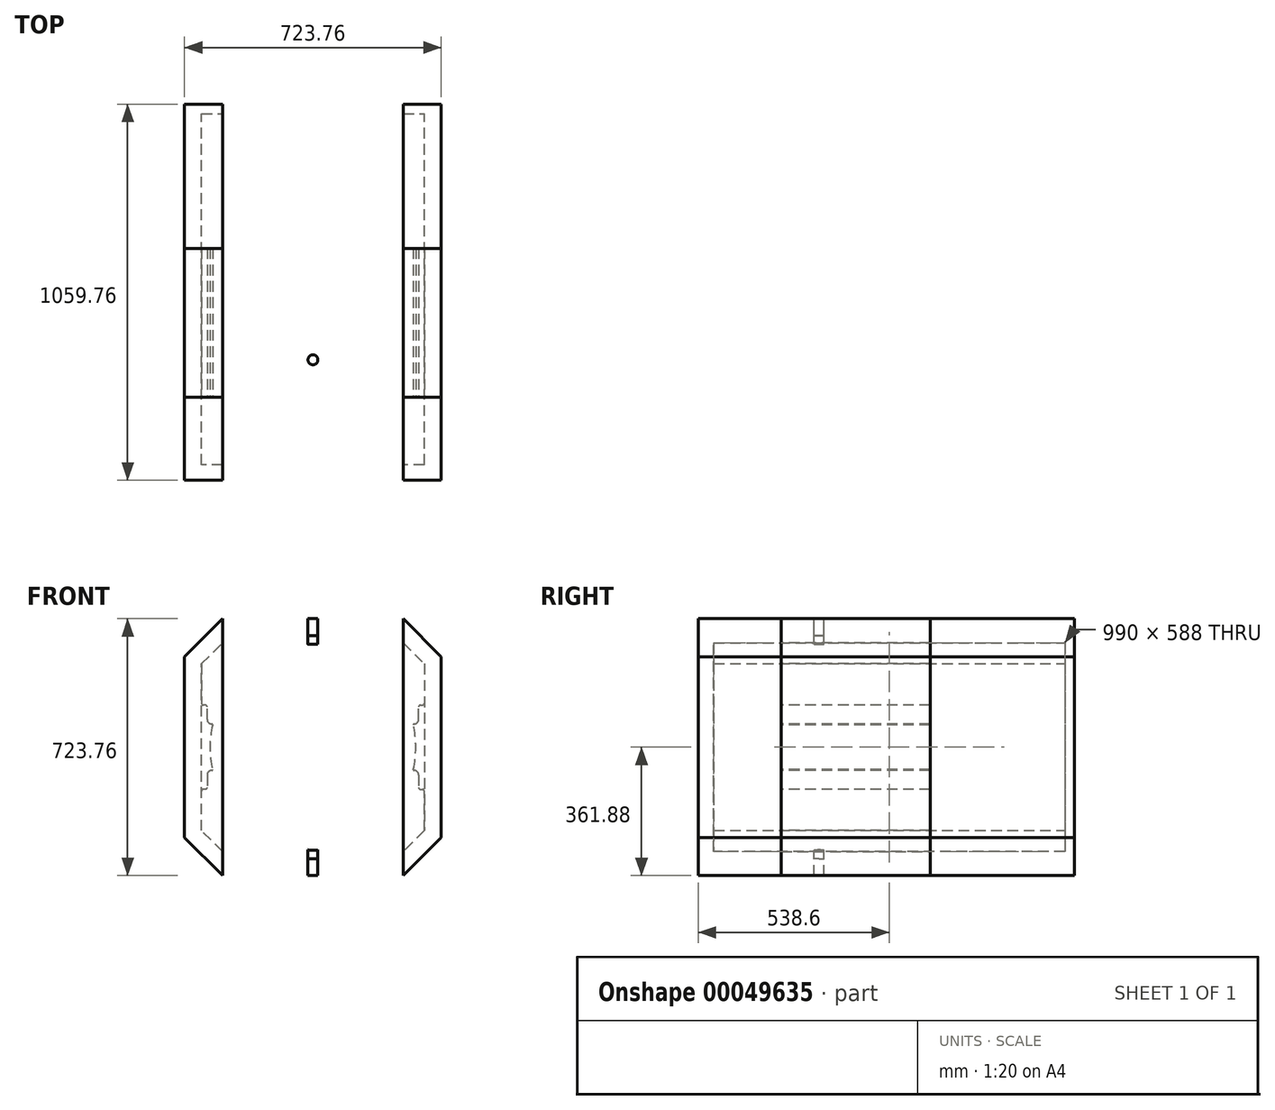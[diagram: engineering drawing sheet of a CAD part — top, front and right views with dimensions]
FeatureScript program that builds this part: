
annotation { "Feature Type Name" : "Feature", "Feature Type Description" : "" }
export const myFeature = defineFeature(function(context is Context, id is Id, definition is map)
    precondition{}
    {
        {
            var Q0;
            Q0=qCreatedBy(makeId("Front.planeOp"),FACE);
            var sketch = newSketch(context, id + "F0", { "sketchPlane" : qUnion([Q0])});
            skLineSegment(sketch, "E0.rect.bottom", {"start": v(-254.77, 361.88) * mm, "end": v(254.77, 361.88) * mm});
            skLineSegment(sketch, "E0.rect.top", {"start": v(-254.77, -361.88) * mm, "end": v(254.77, -361.88) * mm});
            skLineSegment(sketch, "E0.rect.left", {"start": v(-361.88, 254.77) * mm, "end": v(-361.88, -254.77) * mm});
            skLineSegment(sketch, "E0.rect.right", {"start": v(361.88, 254.77) * mm, "end": v(361.88, -254.77) * mm});
            skPoint(sketch, "E0.rect.middle", {"position": v(0, 0) * mm});
            skArc(sketch, "E1", {"start": v(-62.97, -283.02) * mm, "mid": v(-31.67, -288.2) * mm, "end": v(0, -289.94) * mm});
            skLineSegment(sketch, "E2", {"start": v(0, 0) * mm, "end": v(361.88, -361.88) * mm, "construction": true});
            skLineSegment(sketch, "E3", {"start": v(313.88, -234.9) * mm, "end": v(234.9, -313.88) * mm});
            skLineSegment(sketch, "E4", {"start": v(361.88, -254.77) * mm, "end": v(254.77, -361.88) * mm});
            skLineSegment(sketch, "E5.1.0", {"start": v(234.9, 313.88) * mm, "end": v(313.88, 234.9) * mm});
            skLineSegment(sketch, "E5.1.1", {"start": v(254.77, 361.88) * mm, "end": v(361.88, 254.77) * mm});
            skLineSegment(sketch, "E5.2.0", {"start": v(-313.88, 234.9) * mm, "end": v(-234.9, 313.88) * mm});
            skLineSegment(sketch, "E5.2.1", {"start": v(-361.88, 254.77) * mm, "end": v(-254.77, 361.88) * mm});
            skLineSegment(sketch, "E5.3.0", {"start": v(-234.9, -313.88) * mm, "end": v(-313.88, -234.9) * mm});
            skLineSegment(sketch, "E5.3.1", {"start": v(-254.77, -361.88) * mm, "end": v(-361.88, -254.77) * mm});
            skPoint(sketch, "E6.orphan", {"position": v(361.88, 361.88) * mm});
            skPoint(sketch, "E7.orphan", {"position": v(-361.88, 361.88) * mm});
            skPoint(sketch, "E8.orphan", {"position": v(-361.88, -361.88) * mm});
            skLineSegment(sketch, "E9.trimOffspring", {"start": v(-234.9, -313.88) * mm, "end": v(-123.42, -313.88) * mm});
            skCircle(sketch, "E10", {"center": v(0, 0) * mm, "radius": 246.34 * mm, "construction": true});
            skLineSegment(sketch, "E11", {"start": v(0, 0) * mm, "end": v(0, -467.94) * mm, "construction": true});
            skPoint(sketch, "E11.endSnap0", {"position": v(0, -361.88) * mm});
            skLineSegment(sketch, "E12.MirrorCS", {"start": v(-65.4, -284.97) * mm, "end": v(-65.4, -285.17) * mm});
            skLineSegment(sketch, "E13", {"start": v(-78.4, -298.17) * mm, "end": v(-113.42, -298.17) * mm});
            skLineSegment(sketch, "E14", {"start": v(-118.42, -303.17) * mm, "end": v(-118.42, -308.88) * mm});
            skPoint(sketch, "E15.newPointA", {"position": v(-65.4, -313.88) * mm});
            skPoint(sketch, "E15.newPointB", {"position": v(-65.4, -298.17) * mm});
            skArc(sketch, "E15.filletArc", {"start": v(-78.4, -298.17) * mm, "mid": v(-69.2, -294.37) * mm, "end": v(-65.4, -285.17) * mm});
            skPoint(sketch, "E16.visualSharp", {"position": v(-65.4, -282.47) * mm});
            skArc(sketch, "E16.filletArc", {"start": v(-62.97, -283.02) * mm, "mid": v(-64.65, -283.41) * mm, "end": v(-65.4, -284.97) * mm});
            skPoint(sketch, "E17.visualSharp", {"position": v(-118.42, -298.17) * mm});
            skArc(sketch, "E17.filletArc", {"start": v(-113.42, -298.17) * mm, "mid": v(-116.96, -299.64) * mm, "end": v(-118.42, -303.17) * mm});
            skArc(sketch, "E18.filletArc", {"start": v(-123.42, -313.88) * mm, "mid": v(-119.89, -312.42) * mm, "end": v(-118.42, -308.88) * mm});
            skPoint(sketch, "E19.trimOffspring.end.orphan", {"position": v(65.4, -313.88) * mm});
            skPoint(sketch, "E20.orphan", {"position": v(65.4, -282.47) * mm});
            skArc(sketch, "E21.MirrorCS", {"start": v(62.97, -283.02) * mm, "mid": v(31.67, -288.2) * mm, "end": v(0, -289.94) * mm});
            skLineSegment(sketch, "E22.MirrorCS", {"start": v(234.9, -313.88) * mm, "end": v(123.42, -313.88) * mm});
            skArc(sketch, "E23.MirrorCS", {"start": v(123.42, -313.88) * mm, "mid": v(119.89, -312.42) * mm, "end": v(118.42, -308.88) * mm});
            skLineSegment(sketch, "E24.MirrorCS", {"start": v(118.42, -303.17) * mm, "end": v(118.42, -308.88) * mm});
            skArc(sketch, "E25.MirrorCS", {"start": v(113.42, -298.17) * mm, "mid": v(116.96, -299.64) * mm, "end": v(118.42, -303.17) * mm});
            skArc(sketch, "E26.MirrorCS", {"start": v(62.97, -283.02) * mm, "mid": v(64.65, -283.41) * mm, "end": v(65.4, -284.97) * mm});
            skArc(sketch, "E27.MirrorCS", {"start": v(78.4, -298.17) * mm, "mid": v(69.2, -294.37) * mm, "end": v(65.4, -285.17) * mm});
            skLineSegment(sketch, "E28.MirrorCS", {"start": v(78.4, -298.17) * mm, "end": v(113.42, -298.17) * mm});
            skLineSegment(sketch, "E29.1.0", {"start": v(313.88, -234.9) * mm, "end": v(313.88, -123.42) * mm});
            skPoint(sketch, "E29.1.1", {"position": v(313.88, -65.4) * mm});
            skPoint(sketch, "E29.1.2", {"position": v(298.17, -118.42) * mm});
            skPoint(sketch, "E29.1.3", {"position": v(313.88, 65.4) * mm});
            skArc(sketch, "E29.1.4", {"start": v(283.02, -62.97) * mm, "mid": v(288.2, -31.67) * mm, "end": v(289.94, 0) * mm});
            skLineSegment(sketch, "E29.1.5", {"start": v(313.88, 234.9) * mm, "end": v(313.88, 123.42) * mm});
            skPoint(sketch, "E29.1.6", {"position": v(282.47, -65.4) * mm});
            skPoint(sketch, "E29.1.7", {"position": v(282.47, 65.4) * mm});
            skArc(sketch, "E29.1.8", {"start": v(283.02, 62.97) * mm, "mid": v(288.2, 31.67) * mm, "end": v(289.94, 0) * mm});
            skLineSegment(sketch, "E29.1.9", {"start": v(298.17, 78.4) * mm, "end": v(298.17, 113.42) * mm});
            skPoint(sketch, "E29.1.10", {"position": v(298.17, -65.4) * mm});
            skArc(sketch, "E29.1.11", {"start": v(298.17, 113.42) * mm, "mid": v(299.64, 116.96) * mm, "end": v(303.17, 118.42) * mm});
            skLineSegment(sketch, "E29.1.12", {"start": v(303.17, 118.42) * mm, "end": v(308.88, 118.42) * mm});
            skArc(sketch, "E29.1.13", {"start": v(313.88, 123.42) * mm, "mid": v(312.42, 119.89) * mm, "end": v(308.88, 118.42) * mm});
            skLineSegment(sketch, "E29.1.14", {"start": v(298.17, -78.4) * mm, "end": v(298.17, -113.42) * mm});
            skArc(sketch, "E29.1.15", {"start": v(298.17, 78.4) * mm, "mid": v(294.37, 69.2) * mm, "end": v(285.17, 65.4) * mm});
            skArc(sketch, "E29.1.16", {"start": v(283.02, 62.97) * mm, "mid": v(283.41, 64.65) * mm, "end": v(284.97, 65.4) * mm});
            skArc(sketch, "E29.1.17", {"start": v(298.17, -113.42) * mm, "mid": v(299.64, -116.96) * mm, "end": v(303.17, -118.42) * mm});
            skLineSegment(sketch, "E29.1.18", {"start": v(303.17, -118.42) * mm, "end": v(308.88, -118.42) * mm});
            skArc(sketch, "E29.1.19", {"start": v(313.88, -123.42) * mm, "mid": v(312.42, -119.89) * mm, "end": v(308.88, -118.42) * mm});
            skArc(sketch, "E29.1.20", {"start": v(298.17, -78.4) * mm, "mid": v(294.37, -69.2) * mm, "end": v(285.17, -65.4) * mm});
            skLineSegment(sketch, "E29.2.0", {"start": v(234.9, 313.88) * mm, "end": v(123.42, 313.88) * mm});
            skPoint(sketch, "E29.2.1", {"position": v(65.4, 313.88) * mm});
            skPoint(sketch, "E29.2.2", {"position": v(118.42, 298.17) * mm});
            skPoint(sketch, "E29.2.3", {"position": v(-65.4, 313.88) * mm});
            skArc(sketch, "E29.2.4", {"start": v(62.97, 283.02) * mm, "mid": v(31.67, 288.2) * mm, "end": v(0, 289.94) * mm});
            skLineSegment(sketch, "E29.2.5", {"start": v(-234.9, 313.88) * mm, "end": v(-123.42, 313.88) * mm});
            skPoint(sketch, "E29.2.6", {"position": v(65.4, 282.47) * mm});
            skPoint(sketch, "E29.2.7", {"position": v(-65.4, 282.47) * mm});
            skArc(sketch, "E29.2.8", {"start": v(-62.97, 283.02) * mm, "mid": v(-31.67, 288.2) * mm, "end": v(0, 289.94) * mm});
            skLineSegment(sketch, "E29.2.9", {"start": v(-78.4, 298.17) * mm, "end": v(-113.42, 298.17) * mm});
            skPoint(sketch, "E29.2.10", {"position": v(65.4, 298.17) * mm});
            skArc(sketch, "E29.2.11", {"start": v(-113.42, 298.17) * mm, "mid": v(-116.96, 299.64) * mm, "end": v(-118.42, 303.17) * mm});
            skLineSegment(sketch, "E29.2.12", {"start": v(-118.42, 303.17) * mm, "end": v(-118.42, 308.88) * mm});
            skArc(sketch, "E29.2.13", {"start": v(-123.42, 313.88) * mm, "mid": v(-119.89, 312.42) * mm, "end": v(-118.42, 308.88) * mm});
            skLineSegment(sketch, "E29.2.14", {"start": v(78.4, 298.17) * mm, "end": v(113.42, 298.17) * mm});
            skArc(sketch, "E29.2.15", {"start": v(-78.4, 298.17) * mm, "mid": v(-69.2, 294.37) * mm, "end": v(-65.4, 285.17) * mm});
            skArc(sketch, "E29.2.16", {"start": v(-62.97, 283.02) * mm, "mid": v(-64.65, 283.41) * mm, "end": v(-65.4, 284.97) * mm});
            skArc(sketch, "E29.2.17", {"start": v(113.42, 298.17) * mm, "mid": v(116.96, 299.64) * mm, "end": v(118.42, 303.17) * mm});
            skLineSegment(sketch, "E29.2.18", {"start": v(118.42, 303.17) * mm, "end": v(118.42, 308.88) * mm});
            skArc(sketch, "E29.2.19", {"start": v(123.42, 313.88) * mm, "mid": v(119.89, 312.42) * mm, "end": v(118.42, 308.88) * mm});
            skArc(sketch, "E29.2.20", {"start": v(78.4, 298.17) * mm, "mid": v(69.2, 294.37) * mm, "end": v(65.4, 285.17) * mm});
            skLineSegment(sketch, "E29.3.0", {"start": v(-313.88, 234.9) * mm, "end": v(-313.88, 123.42) * mm});
            skPoint(sketch, "E29.3.1", {"position": v(-313.88, 65.4) * mm});
            skPoint(sketch, "E29.3.2", {"position": v(-298.17, 118.42) * mm});
            skPoint(sketch, "E29.3.3", {"position": v(-313.88, -65.4) * mm});
            skArc(sketch, "E29.3.4", {"start": v(-283.02, 62.97) * mm, "mid": v(-288.2, 31.67) * mm, "end": v(-289.94, 0) * mm});
            skLineSegment(sketch, "E29.3.5", {"start": v(-313.88, -234.9) * mm, "end": v(-313.88, -123.42) * mm});
            skPoint(sketch, "E29.3.6", {"position": v(-282.47, 65.4) * mm});
            skPoint(sketch, "E29.3.7", {"position": v(-282.47, -65.4) * mm});
            skArc(sketch, "E29.3.8", {"start": v(-283.02, -62.97) * mm, "mid": v(-288.2, -31.67) * mm, "end": v(-289.94, 0) * mm});
            skLineSegment(sketch, "E29.3.9", {"start": v(-298.17, -78.4) * mm, "end": v(-298.17, -113.42) * mm});
            skPoint(sketch, "E29.3.10", {"position": v(-298.17, 65.4) * mm});
            skArc(sketch, "E29.3.11", {"start": v(-298.17, -113.42) * mm, "mid": v(-299.64, -116.96) * mm, "end": v(-303.17, -118.42) * mm});
            skLineSegment(sketch, "E29.3.12", {"start": v(-303.17, -118.42) * mm, "end": v(-308.88, -118.42) * mm});
            skArc(sketch, "E29.3.13", {"start": v(-313.88, -123.42) * mm, "mid": v(-312.42, -119.89) * mm, "end": v(-308.88, -118.42) * mm});
            skLineSegment(sketch, "E29.3.14", {"start": v(-298.17, 78.4) * mm, "end": v(-298.17, 113.42) * mm});
            skArc(sketch, "E29.3.15", {"start": v(-298.17, -78.4) * mm, "mid": v(-294.37, -69.2) * mm, "end": v(-285.17, -65.4) * mm});
            skArc(sketch, "E29.3.16", {"start": v(-283.02, -62.97) * mm, "mid": v(-283.41, -64.65) * mm, "end": v(-284.97, -65.4) * mm});
            skArc(sketch, "E29.3.17", {"start": v(-298.17, 113.42) * mm, "mid": v(-299.64, 116.96) * mm, "end": v(-303.17, 118.42) * mm});
            skLineSegment(sketch, "E29.3.18", {"start": v(-303.17, 118.42) * mm, "end": v(-308.88, 118.42) * mm});
            skArc(sketch, "E29.3.19", {"start": v(-313.88, 123.42) * mm, "mid": v(-312.42, 119.89) * mm, "end": v(-308.88, 118.42) * mm});
            skArc(sketch, "E29.3.20", {"start": v(-298.17, 78.4) * mm, "mid": v(-294.37, 69.2) * mm, "end": v(-285.17, 65.4) * mm});
            skLineSegment(sketch, "E30", {"start": v(65.4, -284.97) * mm, "end": v(65.4, -285.17) * mm});
            skLineSegment(sketch, "E31", {"start": v(-285.17, -65.4) * mm, "end": v(-284.97, -65.4) * mm});
            skArc(sketch, "E32", {"start": v(-285.17, 65.4) * mm, "mid": v(-283.55, 64.67) * mm, "end": v(-283.02, 62.97) * mm});
            skLineSegment(sketch, "E33", {"start": v(-65.4, 285.17) * mm, "end": v(-65.4, 284.97) * mm});
            skArc(sketch, "E34", {"start": v(62.97, 283.02) * mm, "mid": v(64.73, 283.48) * mm, "end": v(65.4, 285.17) * mm});
            skLineSegment(sketch, "E35", {"start": v(284.97, 65.4) * mm, "end": v(285.17, 65.4) * mm});
            skArc(sketch, "E36", {"start": v(285.17, -65.4) * mm, "mid": v(283.55, -64.67) * mm, "end": v(283.02, -62.97) * mm});
            skSolve(sketch);
        }
        {
            var Q0;
            Q0=makeQuery(id+"F0.imprint","IMPRINT",FACE,{"disambiguationData":[TD([[makeQuery(id+"F0.imprint","IMPRINT",EDGE,{"derivedFrom":sQuery(id+"F0.wireOp",EDGE,"E0.rect.bottom")}),-1.0]])]});
            extrude(context, id + "F1", {"entities" : qUnion([Q0]), "oppositeDirection" : true, "depth" : 420 * mm});
        }
        {
            var Q0;
            Q0=makeQuery(id+"F1.opExtrude","CAP_FACE",FACE,{"disambiguationData":[OSD([sQuery(id+"F0.wireOp",EDGE,"E0.rect.bottom"),sQuery(id+"F0.wireOp",EDGE,"E0.rect.top"),sQuery(id+"F0.wireOp",EDGE,"E0.rect.left"),sQuery(id+"F0.wireOp",EDGE,"E0.rect.right"),sQuery(id+"F0.wireOp",EDGE,"E1"),sQuery(id+"F0.wireOp",EDGE,"E3"),sQuery(id+"F0.wireOp",EDGE,"E4"),sQuery(id+"F0.wireOp",EDGE,"E5.1.0"),sQuery(id+"F0.wireOp",EDGE,"E5.1.1"),sQuery(id+"F0.wireOp",EDGE,"E5.2.0"),sQuery(id+"F0.wireOp",EDGE,"E5.2.1"),sQuery(id+"F0.wireOp",EDGE,"E5.3.0"),sQuery(id+"F0.wireOp",EDGE,"E5.3.1"),sQuery(id+"F0.wireOp",EDGE,"E9.trimOffspring"),sQuery(id+"F0.wireOp",EDGE,"E12.MirrorCS"),sQuery(id+"F0.wireOp",EDGE,"E13"),sQuery(id+"F0.wireOp",EDGE,"E14"),sQuery(id+"F0.wireOp",EDGE,"E15.filletArc"),sQuery(id+"F0.wireOp",EDGE,"E16.filletArc"),sQuery(id+"F0.wireOp",EDGE,"E17.filletArc"),sQuery(id+"F0.wireOp",EDGE,"E18.filletArc"),sQuery(id+"F0.wireOp",EDGE,"E21.MirrorCS"),sQuery(id+"F0.wireOp",EDGE,"E22.MirrorCS"),sQuery(id+"F0.wireOp",EDGE,"E23.MirrorCS"),sQuery(id+"F0.wireOp",EDGE,"E24.MirrorCS"),sQuery(id+"F0.wireOp",EDGE,"E25.MirrorCS"),sQuery(id+"F0.wireOp",EDGE,"E26.MirrorCS"),sQuery(id+"F0.wireOp",EDGE,"E27.MirrorCS"),sQuery(id+"F0.wireOp",EDGE,"E28.MirrorCS"),sQuery(id+"F0.wireOp",EDGE,"E29.1.0"),sQuery(id+"F0.wireOp",EDGE,"E29.1.4"),sQuery(id+"F0.wireOp",EDGE,"E29.1.5"),sQuery(id+"F0.wireOp",EDGE,"E29.1.8"),sQuery(id+"F0.wireOp",EDGE,"E29.1.9"),sQuery(id+"F0.wireOp",EDGE,"E29.1.11"),sQuery(id+"F0.wireOp",EDGE,"E29.1.12"),sQuery(id+"F0.wireOp",EDGE,"E29.1.13"),sQuery(id+"F0.wireOp",EDGE,"E29.1.14"),sQuery(id+"F0.wireOp",EDGE,"E29.1.15"),sQuery(id+"F0.wireOp",EDGE,"E29.1.16"),sQuery(id+"F0.wireOp",EDGE,"E29.1.17"),sQuery(id+"F0.wireOp",EDGE,"E29.1.18"),sQuery(id+"F0.wireOp",EDGE,"E29.1.19"),sQuery(id+"F0.wireOp",EDGE,"E29.1.20"),sQuery(id+"F0.wireOp",EDGE,"E29.2.0"),sQuery(id+"F0.wireOp",EDGE,"E29.2.4"),sQuery(id+"F0.wireOp",EDGE,"E29.2.5"),sQuery(id+"F0.wireOp",EDGE,"E29.2.8"),sQuery(id+"F0.wireOp",EDGE,"E29.2.9"),sQuery(id+"F0.wireOp",EDGE,"E29.2.11"),sQuery(id+"F0.wireOp",EDGE,"E29.2.12"),sQuery(id+"F0.wireOp",EDGE,"E29.2.13"),sQuery(id+"F0.wireOp",EDGE,"E29.2.14"),sQuery(id+"F0.wireOp",EDGE,"E29.2.15"),sQuery(id+"F0.wireOp",EDGE,"E29.2.16"),sQuery(id+"F0.wireOp",EDGE,"E29.2.17"),sQuery(id+"F0.wireOp",EDGE,"E29.2.18"),sQuery(id+"F0.wireOp",EDGE,"E29.2.19"),sQuery(id+"F0.wireOp",EDGE,"E29.2.20"),sQuery(id+"F0.wireOp",EDGE,"E29.3.0"),sQuery(id+"F0.wireOp",EDGE,"E29.3.4"),sQuery(id+"F0.wireOp",EDGE,"E29.3.5"),sQuery(id+"F0.wireOp",EDGE,"E29.3.8"),sQuery(id+"F0.wireOp",EDGE,"E29.3.9"),sQuery(id+"F0.wireOp",EDGE,"E29.3.11"),sQuery(id+"F0.wireOp",EDGE,"E29.3.12"),sQuery(id+"F0.wireOp",EDGE,"E29.3.13"),sQuery(id+"F0.wireOp",EDGE,"E29.3.14"),sQuery(id+"F0.wireOp",EDGE,"E29.3.15"),sQuery(id+"F0.wireOp",EDGE,"E29.3.16"),sQuery(id+"F0.wireOp",EDGE,"E29.3.17"),sQuery(id+"F0.wireOp",EDGE,"E29.3.18"),sQuery(id+"F0.wireOp",EDGE,"E29.3.19"),sQuery(id+"F0.wireOp",EDGE,"E29.3.20"),sQuery(id+"F0.wireOp",EDGE,"E30"),sQuery(id+"F0.wireOp",EDGE,"E31"),sQuery(id+"F0.wireOp",EDGE,"E32"),sQuery(id+"F0.wireOp",EDGE,"E33"),sQuery(id+"F0.wireOp",EDGE,"E34"),sQuery(id+"F0.wireOp",EDGE,"E35"),sQuery(id+"F0.wireOp",EDGE,"E36")])],"isStart":true});
            var sketch = newSketch(context, id + "F2", { "sketchPlane" : qUnion([Q0])});
            skLineSegment(sketch, "E37.0", {"start": v(-361.88, 254.77) * mm, "end": v(-361.88, -254.77) * mm});
            skLineSegment(sketch, "E37.1", {"start": v(-254.77, -361.88) * mm, "end": v(-361.88, -254.77) * mm});
            skLineSegment(sketch, "E37.2", {"start": v(-361.88, 254.77) * mm, "end": v(-254.77, 361.88) * mm});
            skLineSegment(sketch, "E37.3", {"start": v(-254.77, -361.88) * mm, "end": v(254.77, -361.88) * mm});
            skLineSegment(sketch, "E37.4", {"start": v(-254.77, 361.88) * mm, "end": v(254.77, 361.88) * mm});
            skLineSegment(sketch, "E37.5", {"start": v(254.77, 361.88) * mm, "end": v(361.88, 254.77) * mm});
            skLineSegment(sketch, "E37.6", {"start": v(361.88, 254.77) * mm, "end": v(361.88, -254.77) * mm});
            skLineSegment(sketch, "E37.7", {"start": v(361.88, -254.77) * mm, "end": v(254.77, -361.88) * mm});
            skLineSegment(sketch, "E38.0", {"start": v(-313.88, 234.9) * mm, "end": v(-234.9, 313.88) * mm});
            skLineSegment(sketch, "E39", {"start": v(-234.9, 313.88) * mm, "end": v(234.9, 313.88) * mm});
            skLineSegment(sketch, "E40", {"start": v(234.9, 313.88) * mm, "end": v(313.88, 234.9) * mm});
            skLineSegment(sketch, "E41", {"start": v(313.88, 234.9) * mm, "end": v(313.88, -234.9) * mm});
            skLineSegment(sketch, "E42", {"start": v(313.88, -234.9) * mm, "end": v(234.9, -313.88) * mm});
            skLineSegment(sketch, "E43", {"start": v(234.9, -313.88) * mm, "end": v(-234.9, -313.88) * mm});
            skLineSegment(sketch, "E44", {"start": v(-234.9, -313.88) * mm, "end": v(-313.88, -234.9) * mm});
            skLineSegment(sketch, "E45", {"start": v(-313.88, -234.9) * mm, "end": v(-313.88, 234.9) * mm});
            skSolve(sketch);
        }
        {
            var Q0;
            Q0=makeQuery(id+"F2.imprint","IMPRINT",FACE,{"disambiguationData":[TD([[makeQuery(id+"F2.imprint","IMPRINT",EDGE,{"derivedFrom":sQuery(id+"F2.wireOp",EDGE,"E37.0")}),1.0]])]});
            extrude(context, id + "F3", {"entities" : qUnion([Q0]), "depth" : 190 * mm, "hasSecondDirection" : true, "secondDirectionOppositeDirection" : true, "secondDirectionDepth" : (190 * 2 + 420) * mm});
        }
        {
            var Q0;
            Q0=makeQuery(id+"F3.opExtrude","CAP_FACE",FACE,{"disambiguationData":[OSD([sQuery(id+"F2.wireOp",EDGE,"E37.0"),sQuery(id+"F2.wireOp",EDGE,"E37.1"),sQuery(id+"F2.wireOp",EDGE,"E37.2"),sQuery(id+"F2.wireOp",EDGE,"E37.3"),sQuery(id+"F2.wireOp",EDGE,"E37.4"),sQuery(id+"F2.wireOp",EDGE,"E37.5"),sQuery(id+"F2.wireOp",EDGE,"E37.6"),sQuery(id+"F2.wireOp",EDGE,"E37.7"),sQuery(id+"F2.wireOp",EDGE,"E38.0"),sQuery(id+"F2.wireOp",EDGE,"E39"),sQuery(id+"F2.wireOp",EDGE,"E40"),sQuery(id+"F2.wireOp",EDGE,"E41"),sQuery(id+"F2.wireOp",EDGE,"E42"),sQuery(id+"F2.wireOp",EDGE,"E43"),sQuery(id+"F2.wireOp",EDGE,"E44"),sQuery(id+"F2.wireOp",EDGE,"E45")])],"isStart":false});
            var sketch = newSketch(context, id + "F4", { "sketchPlane" : qUnion([Q0])});
            skLineSegment(sketch, "E46", {"start": v(-361.88, 254.77) * mm, "end": v(-254.77, 361.88) * mm});
            skLineSegment(sketch, "E47", {"start": v(-254.77, 361.88) * mm, "end": v(254.77, 361.88) * mm});
            skLineSegment(sketch, "E48", {"start": v(254.77, 361.88) * mm, "end": v(361.88, 254.77) * mm});
            skLineSegment(sketch, "E49", {"start": v(361.88, 254.77) * mm, "end": v(361.88, -254.77) * mm});
            skLineSegment(sketch, "E50", {"start": v(361.88, -254.77) * mm, "end": v(254.77, -361.88) * mm});
            skLineSegment(sketch, "E51", {"start": v(254.77, -361.88) * mm, "end": v(-254.77, -361.88) * mm});
            skLineSegment(sketch, "E52", {"start": v(-254.77, -361.88) * mm, "end": v(-361.88, -254.77) * mm});
            skLineSegment(sketch, "E53", {"start": v(-361.88, -254.77) * mm, "end": v(-361.88, 254.77) * mm});
            skCircle(sketch, "E54", {"center": v(0, 0) * mm, "radius": 251.5 * mm});
            skSolve(sketch);
        }
        {
            var Q0;
            Q0=qSketchRegion(id+"F4",true);
            extrude(context, id + "F5", {"entities" : qUnion([Q0]), "operationType" : NewBodyOperationType.ADD, "depth" : (20 * 2.18) * mm});
        }
        {
            var Q0;
            Q0=makeQuery(id+"F3.opExtrude","CAP_FACE",FACE,{"disambiguationData":[OSD([sQuery(id+"F2.wireOp",EDGE,"E37.0"),sQuery(id+"F2.wireOp",EDGE,"E37.1"),sQuery(id+"F2.wireOp",EDGE,"E37.2"),sQuery(id+"F2.wireOp",EDGE,"E37.3"),sQuery(id+"F2.wireOp",EDGE,"E37.4"),sQuery(id+"F2.wireOp",EDGE,"E37.5"),sQuery(id+"F2.wireOp",EDGE,"E37.6"),sQuery(id+"F2.wireOp",EDGE,"E37.7"),sQuery(id+"F2.wireOp",EDGE,"E38.0"),sQuery(id+"F2.wireOp",EDGE,"E39"),sQuery(id+"F2.wireOp",EDGE,"E40"),sQuery(id+"F2.wireOp",EDGE,"E41"),sQuery(id+"F2.wireOp",EDGE,"E42"),sQuery(id+"F2.wireOp",EDGE,"E43"),sQuery(id+"F2.wireOp",EDGE,"E44"),sQuery(id+"F2.wireOp",EDGE,"E45")])],"isStart":true});
            var sketch = newSketch(context, id + "F6", { "sketchPlane" : qUnion([Q0])});
            skLineSegment(sketch, "E55", {"start": v(-361.88, 254.77) * mm, "end": v(-254.77, 361.88) * mm});
            skLineSegment(sketch, "E56", {"start": v(-254.77, 361.88) * mm, "end": v(254.77, 361.88) * mm});
            skLineSegment(sketch, "E57", {"start": v(254.77, 361.88) * mm, "end": v(361.88, 254.77) * mm});
            skLineSegment(sketch, "E58", {"start": v(361.88, 254.77) * mm, "end": v(361.88, -254.77) * mm});
            skLineSegment(sketch, "E59", {"start": v(361.88, -254.77) * mm, "end": v(254.77, -361.88) * mm});
            skLineSegment(sketch, "E60", {"start": v(254.77, -361.88) * mm, "end": v(-254.77, -361.88) * mm});
            skLineSegment(sketch, "E61", {"start": v(-254.77, -361.88) * mm, "end": v(-361.88, -254.77) * mm});
            skLineSegment(sketch, "E62", {"start": v(-361.88, -254.77) * mm, "end": v(-361.88, 254.77) * mm});
            skCircle(sketch, "E63", {"center": v(0, 0) * mm, "radius": 238.5 * mm});
            skSolve(sketch);
        }
        {
            var Q0;
            Q0=qSketchRegion(id+"F6",true);
            extrude(context, id + "F7", {"entities" : qUnion([Q0]), "operationType" : NewBodyOperationType.ADD, "depth" : (12 * 2.18) * mm});
        }
        {
            var Q0;
            Q0=makeQuery(id+"F7.boolean.opBoolean","MERGE",FACE,{"derivedFrom":[makeQuery(id+"F5.boolean.opBoolean","MERGE",FACE,{"derivedFrom":[makeQuery(id+"F3.opExtrude","SWEPT_FACE",FACE,{"disambiguationData":[OSD([sQuery(id+"F2.wireOp",EDGE,"E37.4")])]}),makeQuery(id+"F5.opExtrude","SWEPT_FACE",FACE,{"disambiguationData":[OSD([sQuery(id+"F4.wireOp",EDGE,"E47")])]})]}),makeQuery(id+"F7.opExtrude","SWEPT_FACE",FACE,{"disambiguationData":[OSD([sQuery(id+"F6.wireOp",EDGE,"E56")])]})]});
            var sketch = newSketch(context, id + "F8", { "sketchPlane" : qUnion([Q0])});
            skLineSegment(sketch, "E64", {"start": v(-254.77, 420.3) * mm, "end": v(254.77, 0) * mm, "construction": true});
            skLineSegment(sketch, "E65", {"start": v(254.77, 0) * mm, "end": v(0, 210.15) * mm, "construction": true});
            skLineSegment(sketch, "E66", {"start": v(0, 210.15) * mm, "end": v(0, 418.02) * mm, "construction": true});
            skCircle(sketch, "E67", {"center": v(0, 210.15) * mm, "radius": 14 * mm});
            skCircle(sketch, "E68", {"center": v(0, 314.09) * mm, "radius": 14 * mm});
            skLineSegment(sketch, "E69", {"start": v(0, 210.15) * mm, "end": v(-113.18, 210.15) * mm, "construction": true});
            skCircle(sketch, "E70.MirrorC", {"center": v(0, 106.21) * mm, "radius": 14 * mm});
            skSolve(sketch);
        }
        {
            var Q0;
            Q0=makeQuery(id+"F8.imprint","IMPRINT",FACE,{"disambiguationData":[TD([[makeQuery(id+"F8.imprint","IMPRINT",EDGE,{"derivedFrom":sQuery(id+"F8.wireOp",EDGE,"E70.MirrorC")}),-1.0]])]});
            var Q1;
            Q1=makeQuery(id+"F8.imprint","IMPRINT",FACE,{"disambiguationData":[TD([[makeQuery(id+"F8.imprint","IMPRINT",EDGE,{"derivedFrom":sQuery(id+"F8.wireOp",EDGE,"E67")}),1.0]])]});
            var Q2;
            Q2=makeQuery(id+"F8.imprint","IMPRINT",FACE,{"disambiguationData":[TD([[makeQuery(id+"F8.imprint","IMPRINT",EDGE,{"derivedFrom":sQuery(id+"F8.wireOp",EDGE,"E68")}),1.0]])]});
            extrude(context, id + "F9", {"entities" : qUnion([Q0, Q1, Q2]), "operationType" : NewBodyOperationType.REMOVE, "oppositeDirection" : true, "depth" : 895.83 * mm});
        }
    });
